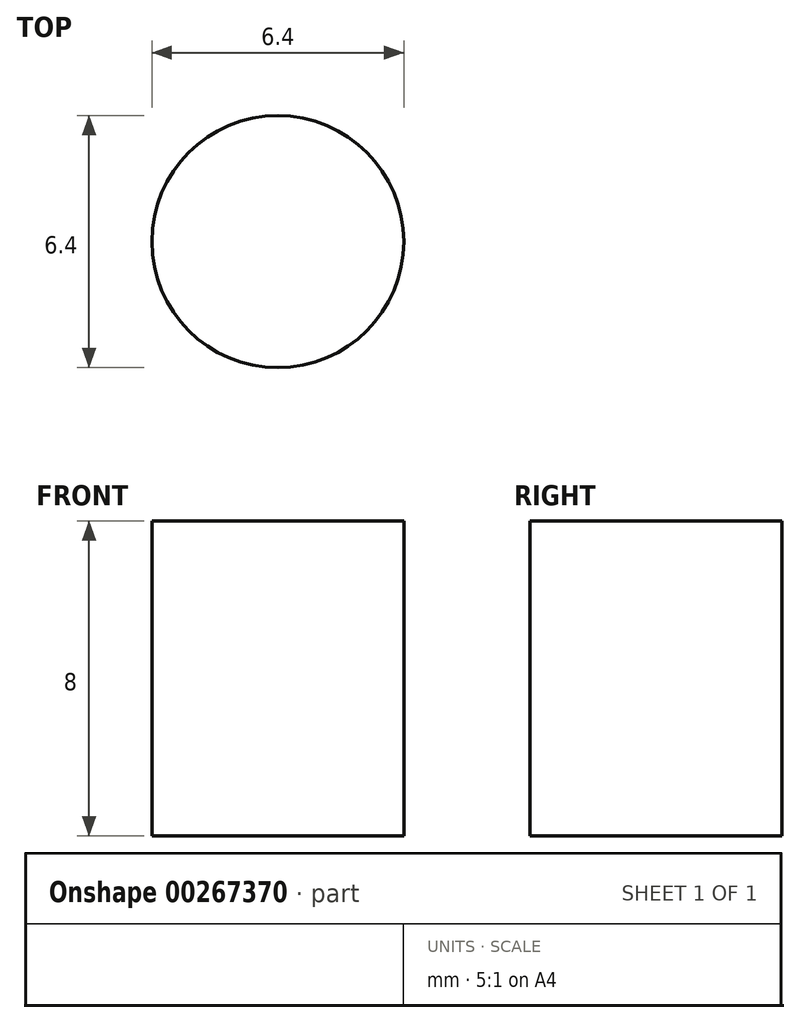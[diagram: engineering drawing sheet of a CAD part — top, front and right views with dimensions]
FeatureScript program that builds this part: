
annotation { "Feature Type Name" : "Feature", "Feature Type Description" : "" }
export const myFeature = defineFeature(function(context is Context, id is Id, definition is map)
    precondition{}
    {
        {
            var Q0;
            Q0=qCreatedBy(makeId("Top.planeOp"),FACE);
            var sketch = newSketch(context, id + "F0", { "sketchPlane" : qUnion([Q0])});
            skCircle(sketch, "E0", {"center": v(-30.11, -4.21) * mm, "radius": 3.2 * mm});
            skSolve(sketch);
        }
        {
            var Q0;
            Q0=makeQuery(id+"F0.imprint","IMPRINT",FACE,{"disambiguationData":[TD([[makeQuery(id+"F0.imprint","IMPRINT",EDGE,{"derivedFrom":sQuery(id+"F0.wireOp",EDGE,"E0")}),1.0]])]});
            extrude(context, id + "F1", {"entities" : qUnion([Q0]), "depth" : 8 * mm});
        }
    });
